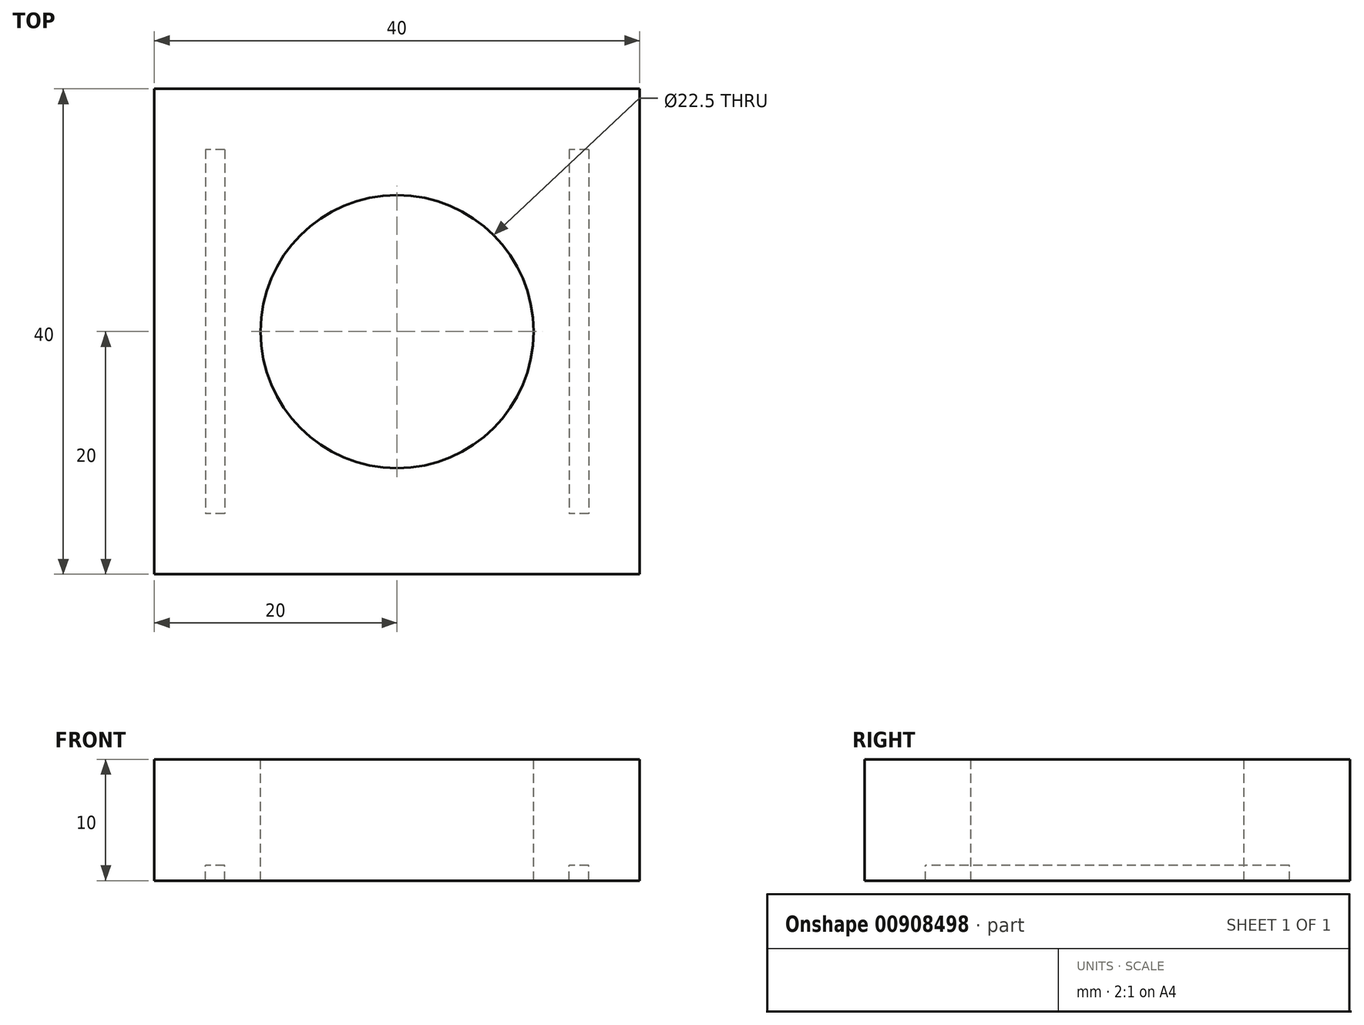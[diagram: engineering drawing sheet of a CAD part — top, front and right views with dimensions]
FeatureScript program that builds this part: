
annotation { "Feature Type Name" : "Feature", "Feature Type Description" : "" }
export const myFeature = defineFeature(function(context is Context, id is Id, definition is map)
    precondition{}
    {
        {
            var Q0;
            Q0=qCreatedBy(makeId("Top.planeOp"),FACE);
            var sketch = newSketch(context, id + "F0", { "sketchPlane" : qUnion([Q0])});
            skLineSegment(sketch, "E0.bottom", {"start": v(20, -20) * mm, "end": v(-20, -20) * mm});
            skLineSegment(sketch, "E0.top", {"start": v(20, 20) * mm, "end": v(-20, 20) * mm});
            skLineSegment(sketch, "E0.left", {"start": v(20, -20) * mm, "end": v(20, 20) * mm});
            skLineSegment(sketch, "E0.right", {"start": v(-20, -20) * mm, "end": v(-20, 20) * mm});
            skPoint(sketch, "E0.middle", {"position": v(0, 0) * mm});
            skSolve(sketch);
        }
        {
            var Q0;
            Q0=makeQuery(id+"F0.imprint","IMPRINT",FACE,{"disambiguationData":[TD([[makeQuery(id+"F0.imprint","IMPRINT",EDGE,{"derivedFrom":sQuery(id+"F0.wireOp",EDGE,"E0.bottom")}),-1.0]])]});
            extrude(context, id + "F1", {"entities" : qUnion([Q0]), "depth" : 10 * mm, "offsetDistance" : 25 * mm});
        }
        {
            var Q0;
            Q0=qCreatedBy(makeId("Top.planeOp"),FACE);
            var sketch = newSketch(context, id + "F2", { "sketchPlane" : qUnion([Q0])});
            skLineSegment(sketch, "E1.bottom", {"start": v(-14.2, 15) * mm, "end": v(-15.8, 15) * mm});
            skLineSegment(sketch, "E1.top", {"start": v(-14.2, -15) * mm, "end": v(-15.8, -15) * mm});
            skLineSegment(sketch, "E1.left", {"start": v(-14.2, 15) * mm, "end": v(-14.2, -15) * mm});
            skLineSegment(sketch, "E1.right", {"start": v(-15.8, 15) * mm, "end": v(-15.8, -15) * mm});
            skPoint(sketch, "E1.middle", {"position": v(-15, 0) * mm});
            skLineSegment(sketch, "E2.bottom", {"start": v(15.8, 15) * mm, "end": v(14.2, 15) * mm});
            skLineSegment(sketch, "E2.top", {"start": v(15.8, -15) * mm, "end": v(14.2, -15) * mm});
            skLineSegment(sketch, "E2.left", {"start": v(15.8, 15) * mm, "end": v(15.8, -15) * mm});
            skLineSegment(sketch, "E2.right", {"start": v(14.2, 15) * mm, "end": v(14.2, -15) * mm});
            skPoint(sketch, "E2.middle", {"position": v(15, 0) * mm});
            skSolve(sketch);
        }
        {
            var Q0;
            Q0=makeQuery(id+"F2.imprint","IMPRINT",FACE,{"disambiguationData":[TD([[makeQuery(id+"F2.imprint","IMPRINT",EDGE,{"derivedFrom":sQuery(id+"F2.wireOp",EDGE,"E1.bottom")}),1.0]])]});
            var Q1;
            Q1=qSketchRegion(id+"F2",true);
            extrude(context, id + "F3", {"entities" : qUnion([Q0, Q1]), "operationType" : NewBodyOperationType.REMOVE, "endBound" : BoundingType.SYMMETRIC, "oppositeDirection" : true, "depth" : 2.5 * mm, "offsetDistance" : 25 * mm});
        }
        {
            var Q0;
            Q0=qCreatedBy(makeId("Top.planeOp"),FACE);
            var sketch = newSketch(context, id + "F4", { "sketchPlane" : qUnion([Q0])});
            skCircle(sketch, "E3", {"center": v(0, 0) * mm, "radius": 11.25 * mm});
            skSolve(sketch);
        }
        {
            var Q0;
            Q0=qSketchRegion(id+"F4",true);
            extrude(context, id + "F5", {"entities" : qUnion([Q0]), "operationType" : NewBodyOperationType.REMOVE, "endBound" : BoundingType.SYMMETRIC, "oppositeDirection" : true, "depth" : 25 * mm, "offsetDistance" : 25 * mm});
        }
    });
